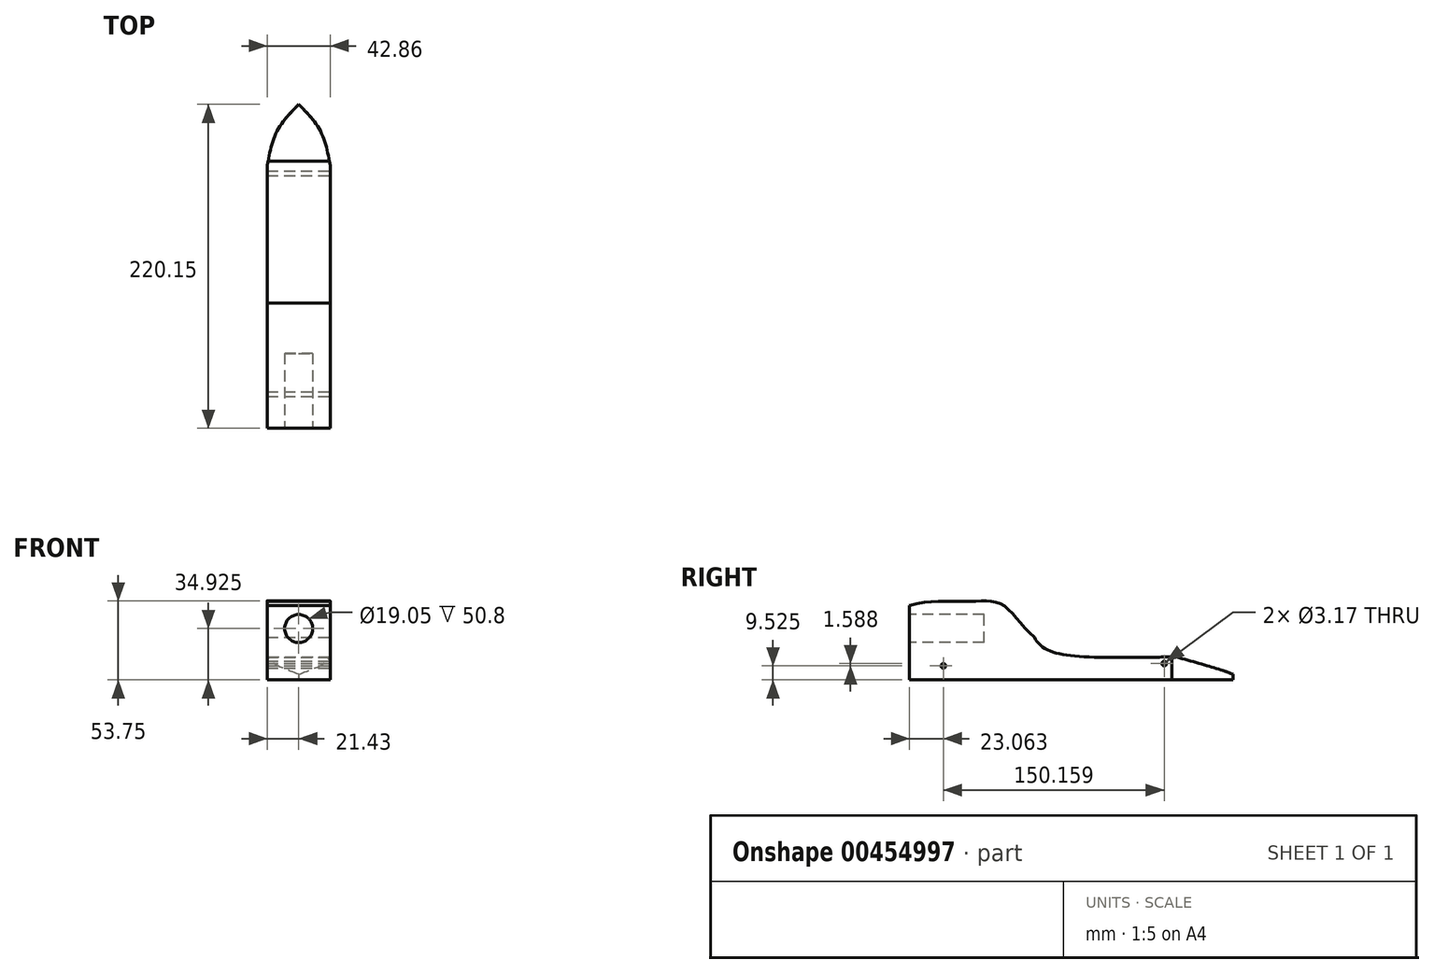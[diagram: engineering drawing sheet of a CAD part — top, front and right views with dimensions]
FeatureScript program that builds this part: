
annotation { "Feature Type Name" : "Feature", "Feature Type Description" : "" }
export const myFeature = defineFeature(function(context is Context, id is Id, definition is map)
    precondition{}
    {
        {
            var Q0;
            Q0=qCreatedBy(makeId("Right.planeOp"),FACE);
            var sketch = newSketch(context, id + "F0", { "sketchPlane" : qUnion([Q0])});
            skLineSegment(sketch, "E0", {"start": v(-152.4, 0) * mm, "end": v(152.4, 0) * mm});
            skLineSegment(sketch, "E1", {"start": v(-152.4, 0) * mm, "end": v(-152.4, 69.85) * mm});
            skLineSegment(sketch, "E2", {"start": v(152.4, 0) * mm, "end": v(152.4, 19.05) * mm});
            skLineSegment(sketch, "E3", {"start": v(152.4, 19.05) * mm, "end": v(-152.4, 69.85) * mm});
            skPoint(sketch, "E4.endSnap0", {"position": v(-152.4, 34.93) * mm});
            skLineSegment(sketch, "E5.0", {"start": v(-95.25, 50.8) * mm, "end": v(-152.4, 50.8) * mm, "construction": true});
            skLineSegment(sketch, "E5.1", {"start": v(-95.25, 50.8) * mm, "end": v(-95.25, 19.05) * mm, "construction": true});
            skLineSegment(sketch, "E5.2", {"start": v(-95.25, 19.05) * mm, "end": v(-152.4, 19.05) * mm, "construction": true});
            skSolve(sketch);
        }
        {
            var Q0;
            Q0=makeQuery(id+"F0.imprint","IMPRINT",FACE,{"disambiguationData":[TD([[makeQuery(id+"F0.imprint","IMPRINT",EDGE,{"derivedFrom":sQuery(id+"F0.wireOp",EDGE,"E0")}),1.0]])]});
            extrude(context, id + "F1", {"entities" : qUnion([Q0]), "depth" : 42.86 * mm, "symmetric" : true});
        }
        {
            var Q0;
            Q0=makeQuery(id+"F1.opExtrude","SWEPT_FACE",FACE,{"disambiguationData":[OSD([sQuery(id+"F0.wireOp",EDGE,"E1")])]});
            var sketch = newSketch(context, id + "F2", { "sketchPlane" : qUnion([Q0])});
            skLineSegment(sketch, "E6", {"start": v(21.43, 34.93) * mm, "end": v(0, 34.93) * mm, "construction": true});
            skCircle(sketch, "E7", {"center": v(0, 34.93) * mm, "radius": 9.53 * mm});
            skSolve(sketch);
        }
        {
            var Q0;
            Q0=makeQuery(id+"F2.imprint","IMPRINT",FACE,{"disambiguationData":[TD([[makeQuery(id+"F2.imprint","IMPRINT",EDGE,{"derivedFrom":sQuery(id+"F2.wireOp",EDGE,"E7")}),1.0]])]});
            var Q1;
            Q1=sQuery(id+"F2.wireOp",EDGE,"E7");
            extrude(context, id + "F3", {"entities" : qUnion([Q0]), "operationType" : NewBodyOperationType.REMOVE, "surfaceEntities" : qUnion([Q1]), "oppositeDirection" : true, "depth" : 50.8 * mm});
        }
        {
            var Q0;
            Q0=makeQuery(id+"F1.opExtrude","CAP_FACE",FACE,{"disambiguationData":[OSD([sQuery(id+"F0.wireOp",EDGE,"E0"),sQuery(id+"F0.wireOp",EDGE,"E1"),sQuery(id+"F0.wireOp",EDGE,"E2"),sQuery(id+"F0.wireOp",EDGE,"E3")])],"isStart":false});
            var sketch = newSketch(context, id + "F4", { "sketchPlane" : qUnion([Q0])});
            skLineSegment(sketch, "E8", {"start": v(-152.4, 34.93) * mm, "end": v(-152.4, 44.45) * mm, "construction": true});
            skLineSegment(sketch, "E9.0", {"start": v(-95.25, 19.05) * mm, "end": v(-152.4, 19.05) * mm, "construction": true});
            skLineSegment(sketch, "E9.1", {"start": v(-95.25, 50.8) * mm, "end": v(-95.25, 19.05) * mm, "construction": true});
            skLineSegment(sketch, "E9.2", {"start": v(-152.4, 50.65) * mm, "end": v(-95.25, 50.8) * mm, "construction": true});
            skLineSegment(sketch, "E10", {"start": v(67.93, 0) * mm, "end": v(67.93, 33.13) * mm, "construction": true});
            skLineSegment(sketch, "E11", {"start": v(-152.4, 44.45) * mm, "end": v(-101.6, 44.45) * mm, "construction": true});
            skLineSegment(sketch, "E12", {"start": v(-101.6, 44.45) * mm, "end": v(-101.6, 25.4) * mm, "construction": true});
            skLineSegment(sketch, "E13", {"start": v(-101.6, 25.4) * mm, "end": v(-152.4, 25.4) * mm, "construction": true});
            skLineSegment(sketch, "E14", {"start": v(-152.4, 0) * mm, "end": v(67.93, 0) * mm});
            skLineSegment(sketch, "E15", {"start": v(67.93, 0) * mm, "end": v(67.93, 15.6) * mm});
            skFitSpline(sketch, "E16", {"points": [v(67.93, 0) * mm, v(67.93, 15.6) * mm], "startDerivative": vector(0, 11.22) * mm, "endDerivative": vector(0, 23.4) * mm});
            skLineSegment(sketch, "E17", {"start": v(67.93, 15.6) * mm, "end": v(67.93, 3.74) * mm});
            skFitSpline(sketch, "E18", {"points": [v(67.93, 15.6) * mm, v(-53.24, 18.47) * mm, v(-67.42, 29) * mm], "startDerivative": vector(-290.66, 2.05) * mm, "endDerivative": vector(-26.68, 56.87) * mm});
            skFitSpline(sketch, "E19", {"points": [v(29.1, 15.57) * mm, v(62.77, 5.63) * mm, v(67.93, 3.74) * mm], "startDerivative": vector(59.01, -16.62) * mm, "endDerivative": vector(19.98, -5) * mm});
            skFitSpline(sketch, "E20", {"points": [v(-67.42, 29) * mm, v(-89.95, 51.48) * mm, v(-112.03, 53.34) * mm, v(-152.4, 50.65) * mm], "startDerivative": vector(-80.72, 69.12) * mm, "endDerivative": vector(-116.5, -32.38) * mm});
            skCircle(sketch, "E21", {"center": v(20.82, 11.11) * mm, "radius": 1.59 * mm});
            skCircle(sketch, "E22", {"center": v(-129.34, 9.53) * mm, "radius": 1.59 * mm});
            skFitSpline(sketch, "E23", {"points": [v(29.1, 15.57) * mm, v(18.17, 18.29) * mm, v(-9.84, 15.22) * mm], "startDerivative": vector(-24.84, 9.32) * mm, "endDerivative": vector(-51.09, -8.55) * mm});
            skSolve(sketch);
        }
        {
            var Q0;
            Q0=makeQuery(id+"F1.opExtrude","SWEPT_FACE",FACE,{"disambiguationData":[OSD([sQuery(id+"F0.wireOp",EDGE,"E0")])]});
            var sketch = newSketch(context, id + "F5", { "sketchPlane" : qUnion([Q0])});
            skLineSegment(sketch, "E24", {"start": v(0, 152.4) * mm, "end": v(0, -152.4) * mm, "construction": true});
            skLineSegment(sketch, "E25", {"start": v(21.43, -57.15) * mm, "end": v(-21.43, -57.15) * mm, "construction": true});
            skLineSegment(sketch, "E26", {"start": v(15.88, 152.4) * mm, "end": v(15.88, 95.25) * mm, "construction": true});
            skLineSegment(sketch, "E27", {"start": v(15.88, 95.25) * mm, "end": v(-15.87, 95.25) * mm, "construction": true});
            skLineSegment(sketch, "E28", {"start": v(-15.87, 95.25) * mm, "end": v(-15.87, 152.4) * mm, "construction": true});
            skLineSegment(sketch, "E29", {"start": v(0, 152.4) * mm, "end": v(-9.53, 152.4) * mm, "construction": true});
            skLineSegment(sketch, "E30", {"start": v(-9.53, 152.4) * mm, "end": v(-9.53, 101.6) * mm, "construction": true});
            skLineSegment(sketch, "E31", {"start": v(-9.52, 101.6) * mm, "end": v(9.53, 101.6) * mm, "construction": true});
            skLineSegment(sketch, "E32", {"start": v(9.53, 101.6) * mm, "end": v(9.53, 152.4) * mm, "construction": true});
            skFitSpline(sketch, "E33", {"points": [v(0, -67.75) * mm, v(14.83, -49.47) * mm, v(21.43, -26.16) * mm], "startDerivative": vector(34.04, 34.47) * mm, "endDerivative": vector(8.88, 48.67) * mm});
            skFitSpline(sketch, "E34.MirrorCS", {"points": [v(0, -67.75) * mm, v(-14.83, -49.47) * mm, v(-21.43, -26.16) * mm], "startDerivative": vector(-34.04, 34.47) * mm, "endDerivative": vector(-8.88, 48.67) * mm});
            skSolve(sketch);
        }
        {
            var Q0;
            {var subQ5=sQuery(id+"F4.wireOp",EDGE,"E14");Q0=makeQuery(id+"F4.imprint","IMPRINT",FACE,{"disambiguationData":[TD([[makeQuery(id+"F4.imprint","IMPRINT",EDGE,{"derivedFrom":subQ5}),1.0]])]});}
            extrude(context, id + "F6", {"entities" : qUnion([Q0]), "operationType" : NewBodyOperationType.INTERSECT, "endBound" : BoundingType.THROUGH_ALL, "oppositeDirection" : true, "depth" : 25.4 * mm});
        }
        {
            var Q0;
            {var subQ4=sQuery(id+"F5.wireOp",EDGE,"E33");Q0=makeQuery(id+"F5.imprint","IMPRINT",FACE,{"disambiguationData":[TD([[makeQuery(id+"F5.imprint","IMPRINT",EDGE,{"derivedFrom":subQ4}),1.0]])]});}
            extrude(context, id + "F7", {"entities" : qUnion([Q0]), "operationType" : NewBodyOperationType.INTERSECT, "endBound" : BoundingType.THROUGH_ALL, "oppositeDirection" : true, "depth" : 25.4 * mm});
        }
    });
